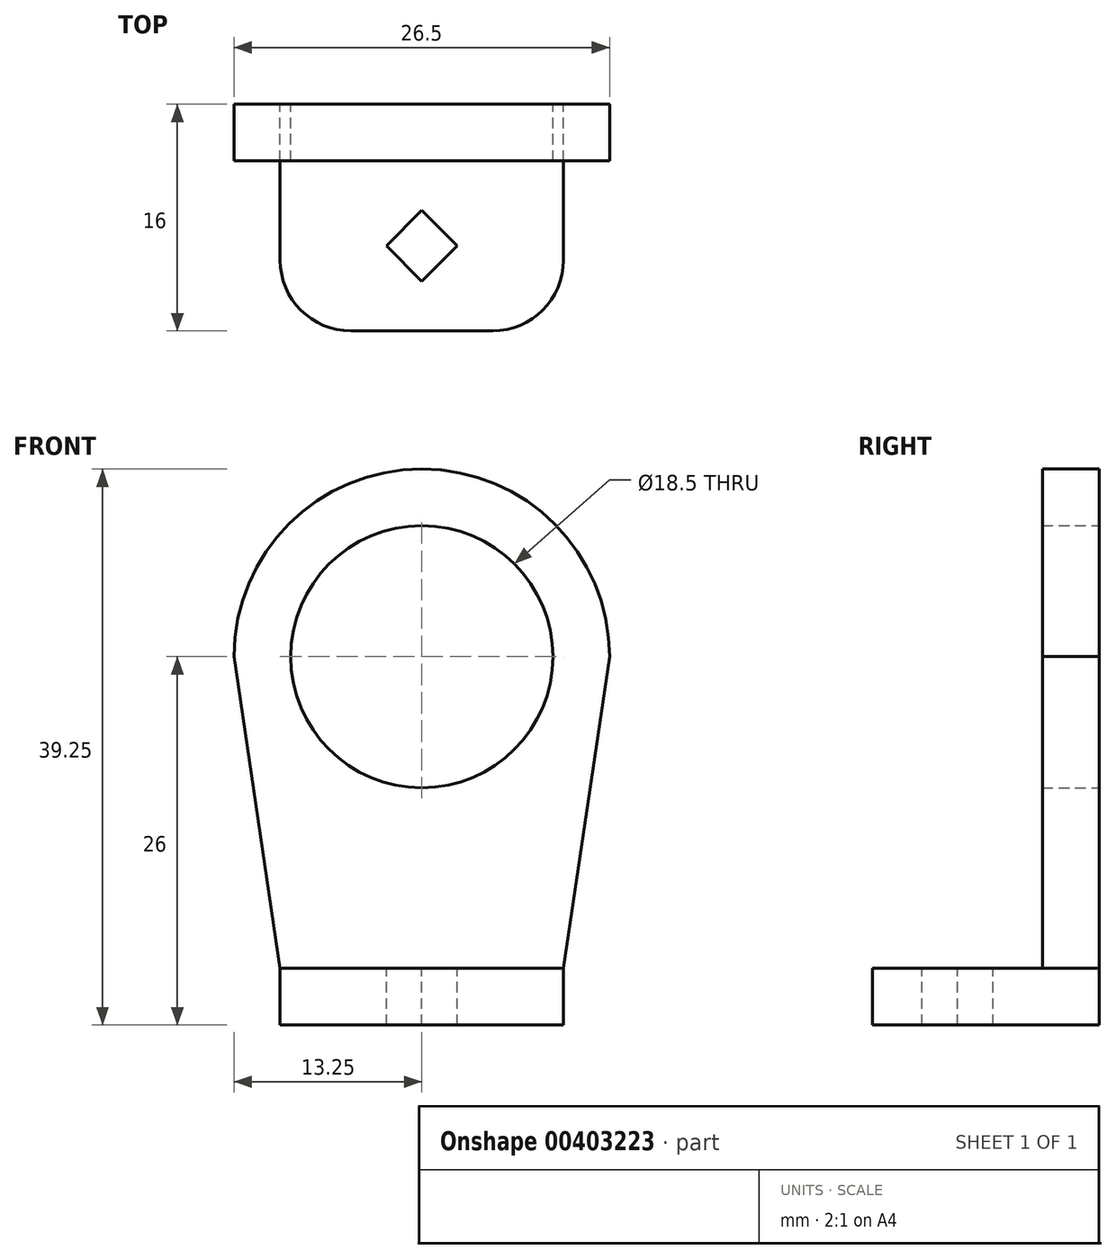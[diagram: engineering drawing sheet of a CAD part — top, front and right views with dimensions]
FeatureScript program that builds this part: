
annotation { "Feature Type Name" : "Feature", "Feature Type Description" : "" }
export const myFeature = defineFeature(function(context is Context, id is Id, definition is map)
    precondition{}
    {
        {
            var Q0;
            Q0=qCreatedBy(makeId("Front.planeOp"),FACE);
            var sketch = newSketch(context, id + "F0", { "sketchPlane" : qUnion([Q0])});
            skCircle(sketch, "E0", {"center": v(0, 26) * mm, "radius": 9.25 * mm});
            skLineSegment(sketch, "E1.bottom", {"start": v(0, 0) * mm, "end": v(-10, 0) * mm});
            skLineSegment(sketch, "E1.top", {"start": v(0, 4) * mm, "end": v(-10, 4) * mm});
            skLineSegment(sketch, "E1.right", {"start": v(-10, 0) * mm, "end": v(-10, 4) * mm});
            skLineSegment(sketch, "E2.bottom", {"start": v(0, 0) * mm, "end": v(10, 0) * mm});
            skLineSegment(sketch, "E2.top", {"start": v(0, 4) * mm, "end": v(10, 4) * mm});
            skLineSegment(sketch, "E2.right", {"start": v(10, 0) * mm, "end": v(10, 4) * mm});
            skArc(sketch, "E3", {"start": v(-13.25, 26) * mm, "mid": v(0, 39.25) * mm, "end": v(13.25, 26) * mm});
            skLineSegment(sketch, "E4", {"start": v(-13.25, 26) * mm, "end": v(-10, 4) * mm});
            skLineSegment(sketch, "E5", {"start": v(13.25, 26) * mm, "end": v(10, 4) * mm});
            skSolve(sketch);
        }
        {
            var Q0;
            Q0=makeQuery(id+"F0.imprint","IMPRINT",FACE,{"disambiguationData":[TD([[makeQuery(id+"F0.imprint","IMPRINT",EDGE,{"derivedFrom":sQuery(id+"F0.wireOp",EDGE,"E1.bottom")}),-1.0]])]});
            extrude(context, id + "F1", {"entities" : qUnion([Q0]), "depth" : 16 * mm});
        }
        {
            var Q0;
            Q0=makeQuery(id+"F0.imprint","IMPRINT",FACE,{"disambiguationData":[TD([[makeQuery(id+"F0.imprint","IMPRINT",EDGE,{"derivedFrom":sQuery(id+"F0.wireOp",EDGE,"E0")}),-1.0]])]});
            extrude(context, id + "F2", {"entities" : qUnion([Q0]), "operationType" : NewBodyOperationType.ADD, "depth" : 4 * mm});
        }
        {
            var Q0;
            Q0=makeQuery(id+"F1.opExtrude","SWEPT_FACE",FACE,{"disambiguationData":[OSD([sQuery(id+"F0.wireOp",EDGE,"E1.top"),sQuery(id+"F0.wireOp",EDGE,"E2.top")])]});
            var sketch = newSketch(context, id + "F3", { "sketchPlane" : qUnion([Q0])});
            skPoint(sketch, "E6.middle", {"position": v(0, -10) * mm});
            skLineSegment(sketch, "E7", {"start": v(0, -10) * mm, "end": v(0, -7.5) * mm});
            skLineSegment(sketch, "E8", {"start": v(0, -10) * mm, "end": v(2.5, -10) * mm});
            skLineSegment(sketch, "E9", {"start": v(0, -10) * mm, "end": v(0, -12.5) * mm});
            skLineSegment(sketch, "E10", {"start": v(0, -10) * mm, "end": v(-2.5, -10) * mm});
            skLineSegment(sketch, "E11", {"start": v(0, -7.5) * mm, "end": v(-2.5, -10) * mm});
            skLineSegment(sketch, "E12", {"start": v(-2.5, -10) * mm, "end": v(0, -12.5) * mm});
            skLineSegment(sketch, "E13", {"start": v(0, -12.5) * mm, "end": v(2.5, -10) * mm});
            skLineSegment(sketch, "E14", {"start": v(2.5, -10) * mm, "end": v(0, -7.5) * mm});
            skSolve(sketch);
        }
        {
            var Q0;
            Q0=makeQuery(id+"F1.opExtrude","CAP_EDGE",EDGE,{"disambiguationData":[OSD([sQuery(id+"F0.wireOp",EDGE,"E1.right")])],"isStart":false});
            var Q1;
            Q1=makeQuery(id+"F1.opExtrude","CAP_EDGE",EDGE,{"disambiguationData":[OSD([sQuery(id+"F0.wireOp",EDGE,"E2.right")])],"isStart":false});
            fillet(context, id + "F4", {"entities" : qUnion([Q0, Q1]), "radius" : 5 * mm, "tangentPropagation" : true, "allowEdgeOverflow" : false});
        }
        {
            var Q0;
            Q0=makeQuery(id+"F3.imprint","IMPRINT",FACE,{"disambiguationData":[TD([[makeQuery(id+"F3.imprint","IMPRINT",EDGE,{"derivedFrom":sQuery(id+"F3.wireOp",EDGE,"E7")}),1.0]])]});
            var Q1;
            Q1=makeQuery(id+"F3.imprint","IMPRINT",FACE,{"disambiguationData":[TD([[makeQuery(id+"F3.imprint","IMPRINT",EDGE,{"derivedFrom":sQuery(id+"F3.wireOp",EDGE,"E9")}),-1.0]])]});
            var Q2;
            Q2=makeQuery(id+"F3.imprint","IMPRINT",FACE,{"disambiguationData":[TD([[makeQuery(id+"F3.imprint","IMPRINT",EDGE,{"derivedFrom":sQuery(id+"F3.wireOp",EDGE,"E8")}),-1.0]])]});
            var Q3;
            Q3=makeQuery(id+"F3.imprint","IMPRINT",FACE,{"disambiguationData":[TD([[makeQuery(id+"F3.imprint","IMPRINT",EDGE,{"derivedFrom":sQuery(id+"F3.wireOp",EDGE,"E7")}),-1.0]])]});
            extrude(context, id + "F5", {"entities" : qUnion([Q0, Q1, Q2, Q3]), "operationType" : NewBodyOperationType.REMOVE, "oppositeDirection" : true, "depth" : 4 * mm});
        }
    });
